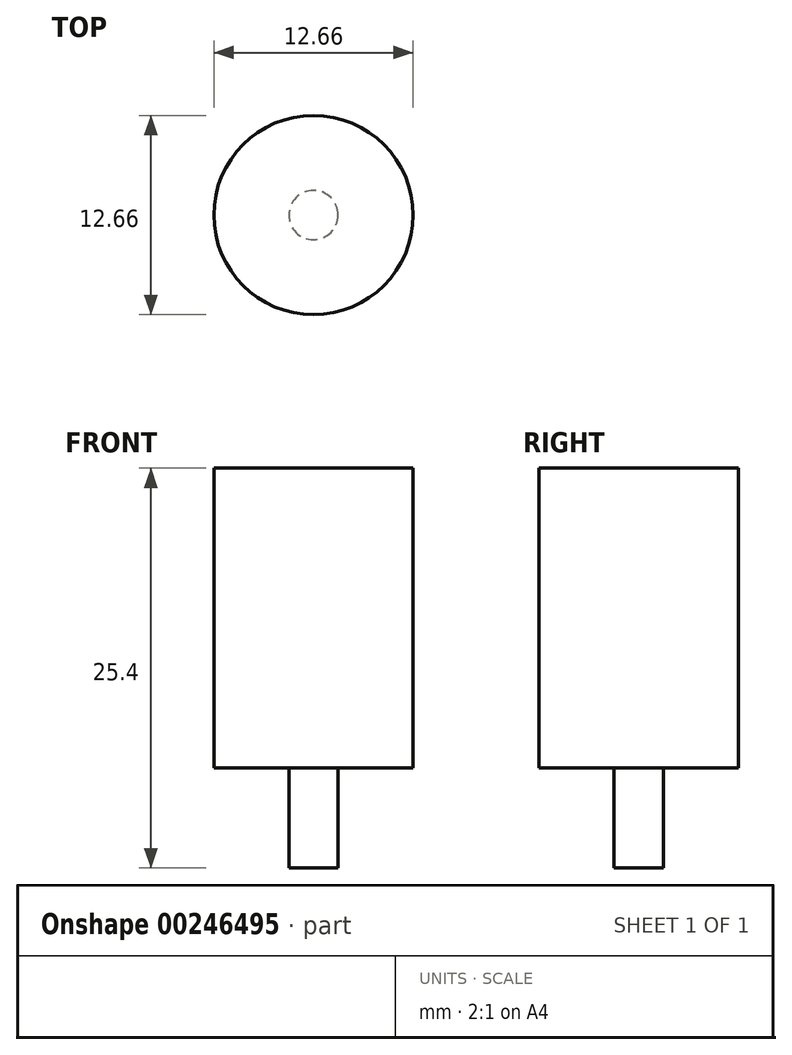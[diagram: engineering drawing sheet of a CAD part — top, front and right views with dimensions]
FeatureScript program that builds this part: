
annotation { "Feature Type Name" : "Feature", "Feature Type Description" : "" }
export const myFeature = defineFeature(function(context is Context, id is Id, definition is map)
    precondition{}
    {
        {
            var Q0;
            Q0=qCreatedBy(makeId("Top.planeOp"),FACE);
            var sketch = newSketch(context, id + "F0", { "sketchPlane" : qUnion([Q0])});
            skCircle(sketch, "E0", {"center": v(0, 0) * mm, "radius": 6.33 * mm});
            skSolve(sketch);
        }
        {
            var Q0;
            Q0=makeQuery(id+"F0.imprint","IMPRINT",FACE,{"disambiguationData":[TD([[makeQuery(id+"F0.imprint","IMPRINT",EDGE,{"derivedFrom":sQuery(id+"F0.wireOp",EDGE,"E0")}),1.0]])]});
            extrude(context, id + "F1", {"entities" : qUnion([Q0]), "depth" : 19.05 * mm});
        }
        {
            var Q0;
            Q0=qCreatedBy(makeId("Top.planeOp"),FACE);
            var sketch = newSketch(context, id + "F2", { "sketchPlane" : qUnion([Q0])});
            skCircle(sketch, "E1", {"center": v(0, 0) * mm, "radius": 1.57 * mm});
            skSolve(sketch);
        }
        {
            var Q0;
            Q0=makeQuery(id+"F2.imprint","IMPRINT",FACE,{"disambiguationData":[TD([[makeQuery(id+"F2.imprint","IMPRINT",EDGE,{"derivedFrom":sQuery(id+"F2.wireOp",EDGE,"E1")}),1.0]])]});
            extrude(context, id + "F3", {"entities" : qUnion([Q0]), "operationType" : NewBodyOperationType.ADD, "oppositeDirection" : true, "depth" : 6.35 * mm});
        }
    });
